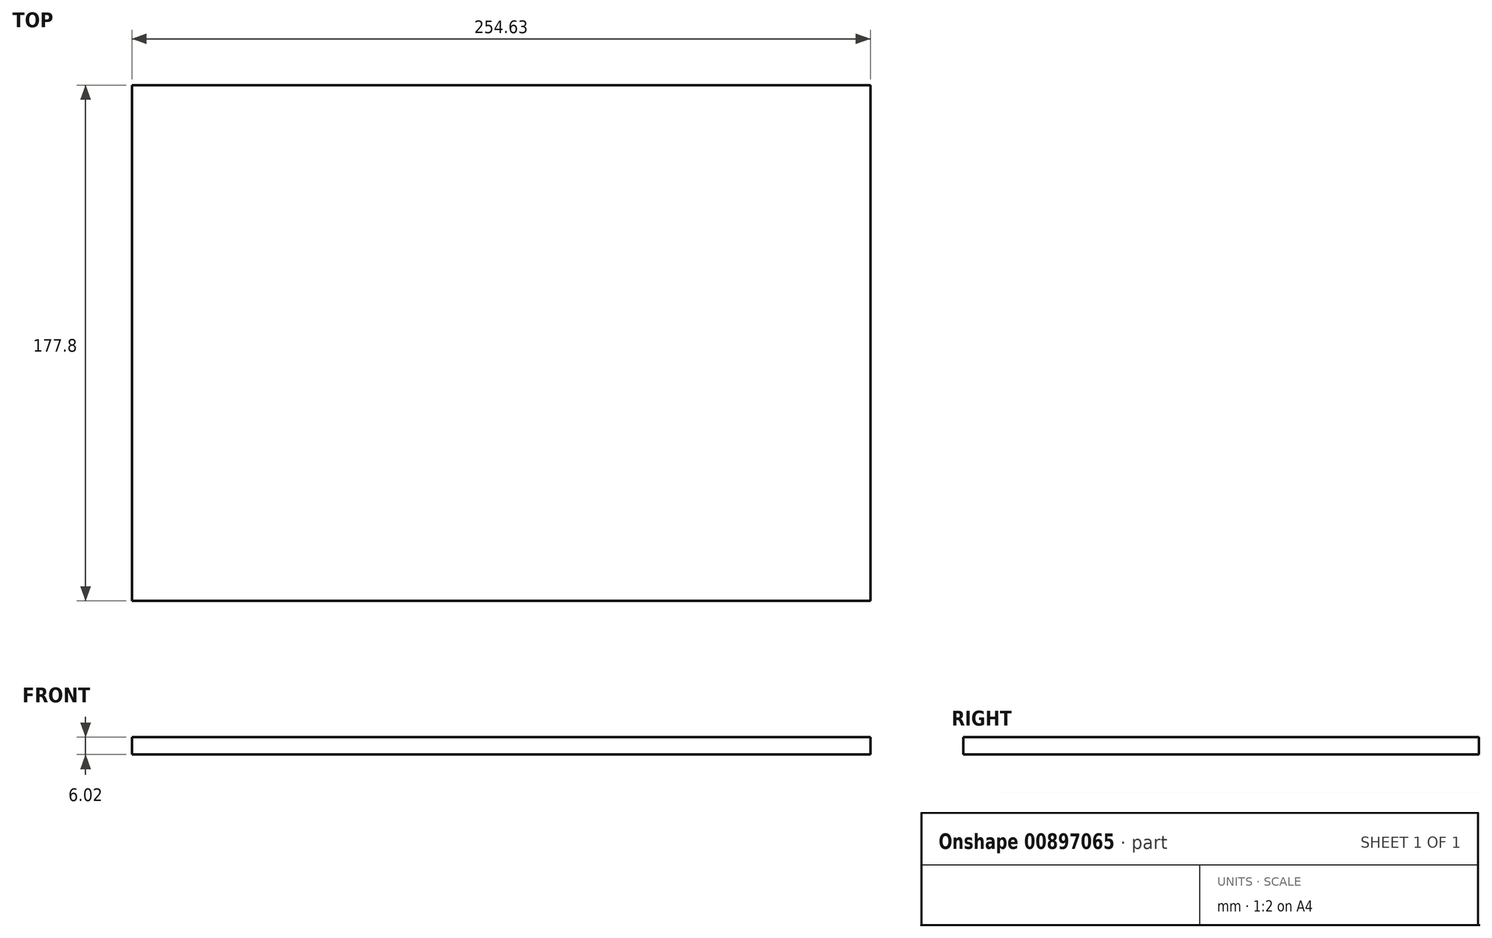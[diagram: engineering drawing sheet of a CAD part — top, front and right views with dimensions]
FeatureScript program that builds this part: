
annotation { "Feature Type Name" : "Feature", "Feature Type Description" : "" }
export const myFeature = defineFeature(function(context is Context, id is Id, definition is map)
    precondition{}
    {
        {
            var Q0;
            Q0=qCreatedBy(makeId("Top.planeOp"),FACE);
            var sketch = newSketch(context, id + "F0", { "sketchPlane" : qUnion([Q0])});
            skLineSegment(sketch, "E0.bottom", {"start": v(0, 0) * mm, "end": v(254.63, 0) * mm});
            skLineSegment(sketch, "E0.top", {"start": v(0, 177.8) * mm, "end": v(254.64, 177.8) * mm});
            skLineSegment(sketch, "E0.left", {"start": v(0, 0) * mm, "end": v(0, 177.8) * mm});
            skLineSegment(sketch, "E0.right", {"start": v(254.64, 0) * mm, "end": v(254.64, 177.8) * mm});
            skSolve(sketch);
        }
        {
            var Q0;
            Q0 = qSketchRegion(id + "F0", true);
            extrude(context, id + "F1", {"entities" : qUnion([Q0]), "depth" : 6.02 * mm, "offsetDistance" : 25.4 * mm});
        }
    });
